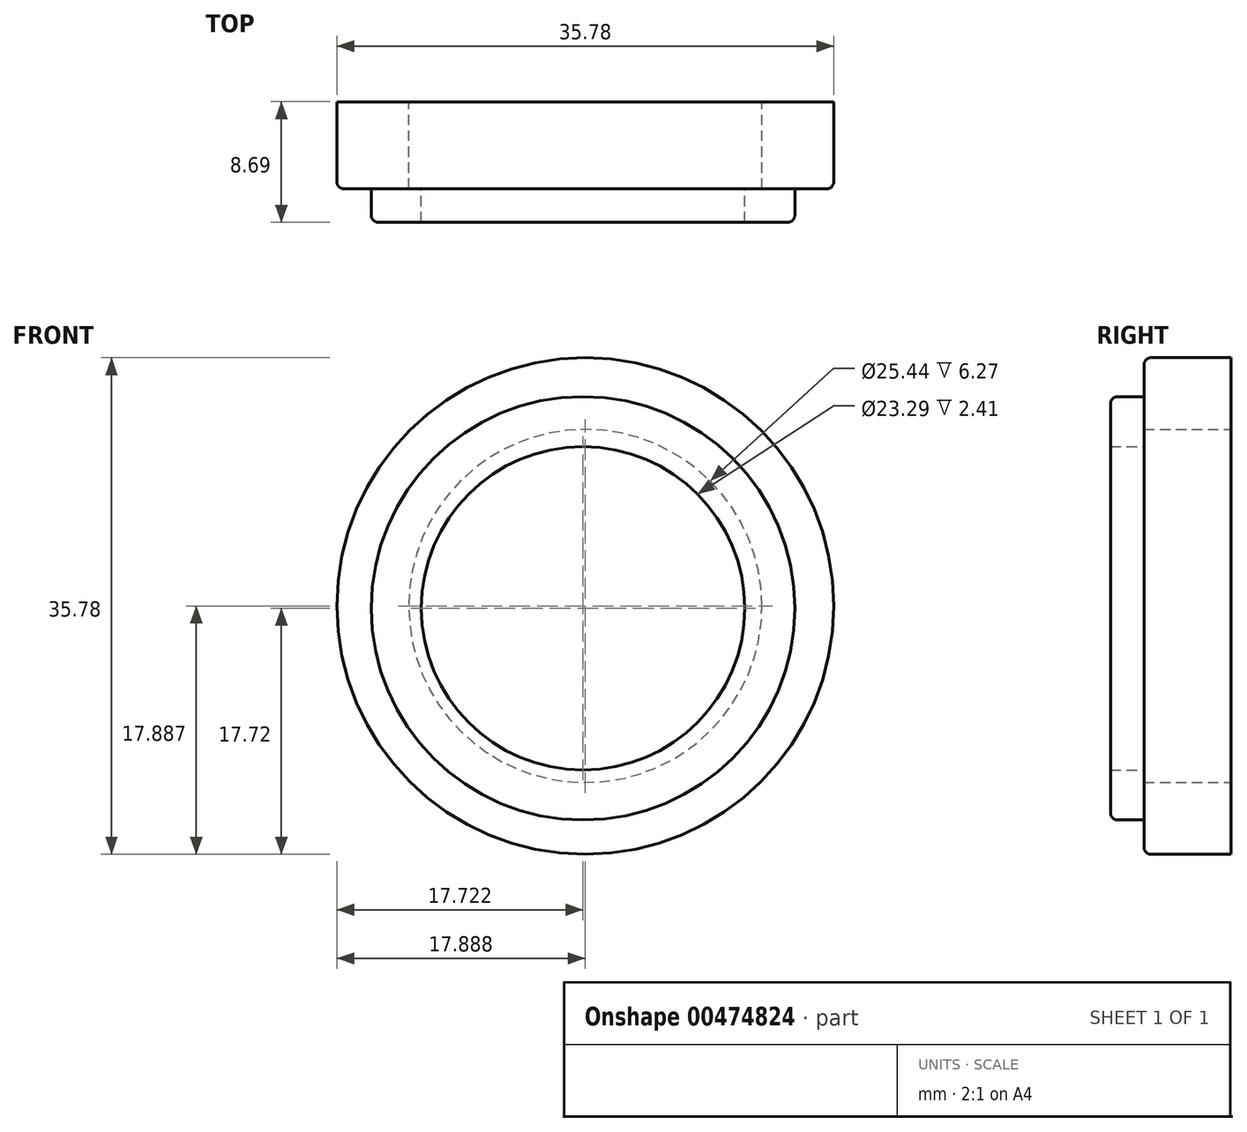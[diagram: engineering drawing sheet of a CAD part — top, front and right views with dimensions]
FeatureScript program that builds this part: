
annotation { "Feature Type Name" : "Feature", "Feature Type Description" : "" }
export const myFeature = defineFeature(function(context is Context, id is Id, definition is map)
    precondition{}
    {
        {
            var Q0;
            Q0=qCreatedBy(makeId("Front.planeOp"),FACE);
            var sketch = newSketch(context, id + "F0", { "sketchPlane" : qUnion([Q0])});
            skLineSegment(sketch, "E0", {"start": v(-42.86, 53.62) * mm, "end": v(-42.86, 13.18) * mm, "construction": true});
            skLineSegment(sketch, "E1", {"start": v(-68.87, 34.82) * mm, "end": v(-7.17, 34.82) * mm, "construction": true});
            skCircle(sketch, "E2", {"center": v(-42.86, 33.4) * mm, "radius": 17.9 * mm});
            skCircle(sketch, "E3", {"center": v(-42.86, 33.4) * mm, "radius": 12.72 * mm});
            skSolve(sketch);
        }
        {
            var Q0;
            Q0=makeQuery(id+"F0.imprint","IMPRINT",FACE,{"disambiguationData":[TD([[makeQuery(id+"F0.imprint","IMPRINT",EDGE,{"derivedFrom":sQuery(id+"F0.wireOp",EDGE,"E2")}),1.0]])]});
            extrude(context, id + "F1", {"entities" : qUnion([Q0]), "endBound" : BoundingType.SYMMETRIC, "depth" : 6.27 * mm});
        }
        {
            var Q0;
            Q0=makeQuery(id+"F1.opExtrude","CAP_FACE",FACE,{"disambiguationData":[OSD([sQuery(id+"F0.wireOp",EDGE,"E2"),sQuery(id+"F0.wireOp",EDGE,"E3")])],"isStart":false});
            cPlane(context, id + "F2", {"entities" : qUnion([Q0]), "cplaneType" : CPlaneType.OFFSET, "offset" : 0 * mm, "oppositeDirection" : true, "width" : 150 * mm, "height" : 150 * mm});
        }
        {
            var Q0;
            Q0=qCreatedBy(id+"F2.planeOp",FACE);
            var sketch = newSketch(context, id + "F3", { "sketchPlane" : qUnion([Q0])});
            skCircle(sketch, "E4", {"center": v(-43.03, 33.23) * mm, "radius": 15.25 * mm});
            skCircle(sketch, "E5", {"center": v(-43.03, 33.23) * mm, "radius": 11.64 * mm});
            skSolve(sketch);
        }
        {
            var Q0;
            Q0=makeQuery(id+"F3.imprint","IMPRINT",FACE,{"disambiguationData":[TD([[makeQuery(id+"F3.imprint","IMPRINT",EDGE,{"derivedFrom":sQuery(id+"F3.wireOp",EDGE,"E4")}),1.0]])]});
            extrude(context, id + "F4", {"entities" : qUnion([Q0]), "operationType" : NewBodyOperationType.ADD, "depth" : 2.41 * mm});
        }
        {
            var Q0;
            Q0=makeQuery(id+"F4.opExtrude","CAP_EDGE",EDGE,{"disambiguationData":[OSD([sQuery(id+"F3.wireOp",EDGE,"E4")])],"isStart":false});
            var Q1;
            Q1=makeQuery(id+"F1.opExtrude","CAP_EDGE",EDGE,{"disambiguationData":[OSD([sQuery(id+"F0.wireOp",EDGE,"E2")])],"isStart":false});
            fillet(context, id + "F5", {"entities" : qUnion([Q0, Q1]), "radius" : 0.5 * mm, "tangentPropagation" : true, "allowEdgeOverflow" : false});
        }
    });
